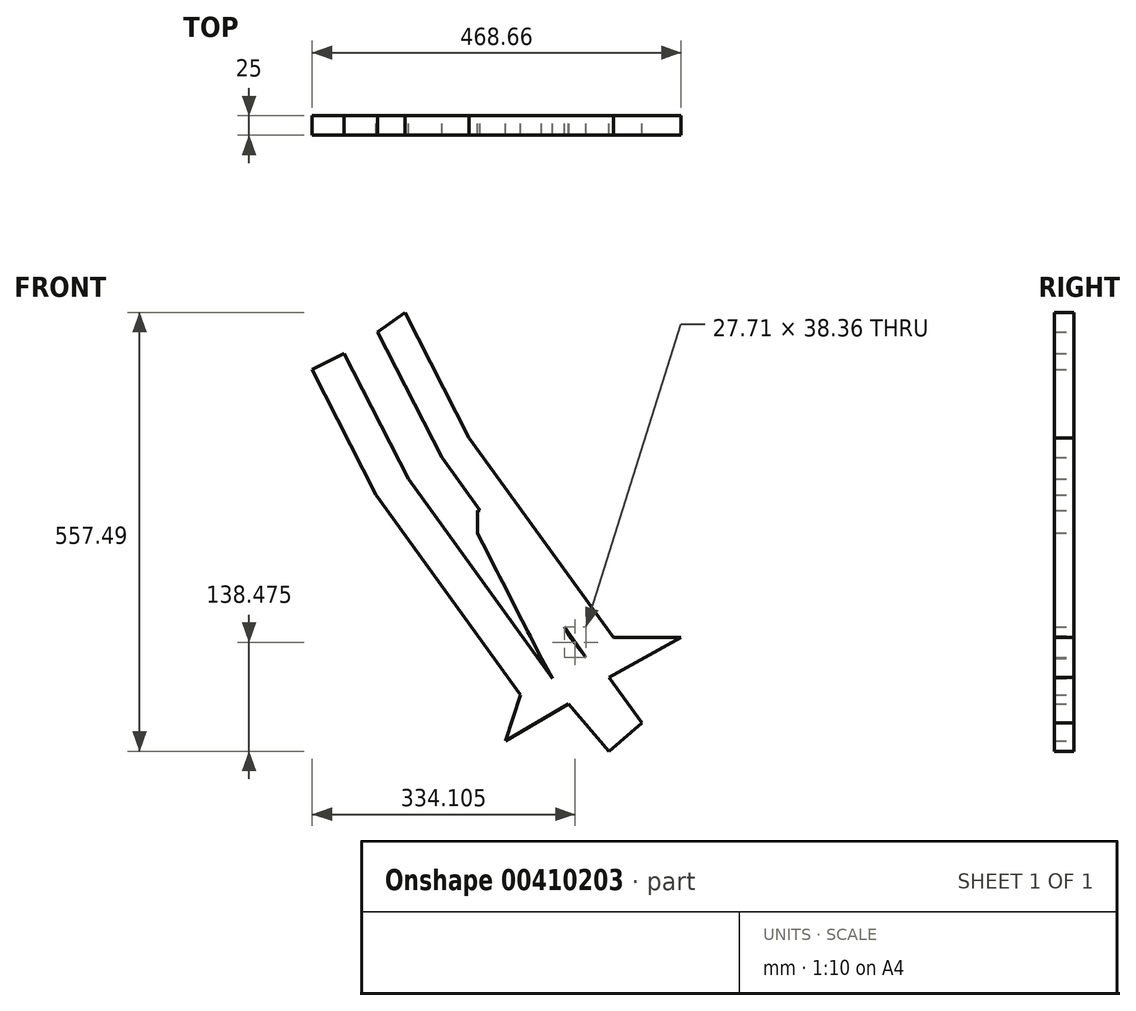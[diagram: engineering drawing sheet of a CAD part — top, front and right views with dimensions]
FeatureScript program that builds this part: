
annotation { "Feature Type Name" : "Feature", "Feature Type Description" : "" }
export const myFeature = defineFeature(function(context is Context, id is Id, definition is map)
    precondition{}
    {
        {
            var Q0;
            Q0=qCreatedBy(makeId("Front.planeOp"),FACE);
            var sketch = newSketch(context, id + "F0", { "sketchPlane" : qUnion([Q0])});
            skLineSegment(sketch, "E0", {"start": v(-19.96, 16.8) * mm, "end": v(14.76, 16.8) * mm});
            skLineSegment(sketch, "E1", {"start": v(14.76, 16.8) * mm, "end": v(-19.96, -11.65) * mm});
            skLineSegment(sketch, "E2", {"start": v(-19.96, -11.65) * mm, "end": v(-19.96, 16.8) * mm});
            skSolve(sketch);
        }
        {
            var Q0;
            Q0=makeQuery(id+"F0.imprint","IMPRINT",FACE,{"disambiguationData":[TD([[makeQuery(id+"F0.imprint","IMPRINT",EDGE,{"derivedFrom":sQuery(id+"F0.wireOp",EDGE,"E0")}),-1.0]])]});
            var sketch = newSketch(context, id + "F1", { "sketchPlane" : qUnion([Q0])});
            skLineSegment(sketch, "E3", {"start": v(14.55, 17.3) * mm, "end": v(36.66, -10.2) * mm});
            skLineSegment(sketch, "E4", {"start": v(36.66, -10.2) * mm, "end": v(71.37, 14.86) * mm});
            skLineSegment(sketch, "E5", {"start": v(71.37, 14.86) * mm, "end": v(157.36, 14.86) * mm});
            skLineSegment(sketch, "E6", {"start": v(157.36, 14.86) * mm, "end": v(65.78, -35.68) * mm});
            skLineSegment(sketch, "E7", {"start": v(65.78, -35.68) * mm, "end": v(107.53, -93.46) * mm});
            skLineSegment(sketch, "E8", {"start": v(107.53, -93.46) * mm, "end": v(65.75, -129.5) * mm});
            skLineSegment(sketch, "E9", {"start": v(65.75, -129.5) * mm, "end": v(14.08, -69.6) * mm});
            skLineSegment(sketch, "E10", {"start": v(14.08, -69.6) * mm, "end": v(-65.47, -116.32) * mm});
            skLineSegment(sketch, "E11", {"start": v(-65.47, -116.32) * mm, "end": v(-46.58, -57.93) * mm});
            skLineSegment(sketch, "E12", {"start": v(-46.58, -57.93) * mm, "end": v(-5.79, -37.1) * mm});
            skLineSegment(sketch, "E13", {"start": v(-5.79, -37.1) * mm, "end": v(-19.96, -11.65) * mm});
            skLineSegment(sketch, "E14", {"start": v(-19.96, -11.65) * mm, "end": v(14.87, 16.9) * mm});
            skSolve(sketch);
        }
        {
            var Q0;
            Q0 = qSketchRegion(id + "F1", true);
            extrude(context, id + "F2", {"entities" : qUnion([Q0]), "depth" : 25 * mm});
        }
        {
            var Q0;
            Q0 = qSketchRegion(id + "F0", true);
            extrude(context, id + "F3", {"entities" : qUnion([Q0]), "operationType" : NewBodyOperationType.ADD, "depth" : 25 * mm});
        }
        {
            var Q0;
            Q0=makeQuery(id+"F2.opExtrude","SWEPT_FACE",FACE,{"disambiguationData":[OSD([sQuery(id+"F1.wireOp",EDGE,"E4")])]});
            var Q1;
            Q1=makeQuery(id+"F2.opExtrude","SWEPT_FACE",FACE,{"disambiguationData":[OSD([sQuery(id+"F1.wireOp",EDGE,"E12")])]});
            extrude(context, id + "F4", {"entities" : qUnion([Q0, Q1]), "operationType" : NewBodyOperationType.ADD, "depth" : 313 * mm});
        }
        {
            var Q0;
            Q0=makeQuery(id+"F4.opExtrude","CAP_FACE",FACE,{"disambiguationData":[OSD([sQuery(id+"F1.wireOp",EDGE,"E4")])],"isStart":false});
            var sketch = newSketch(context, id + "F5", { "sketchPlane" : qUnion([Q0])});
            skLineSegment(sketch, "E15", {"start": v(23.74, 0) * mm, "end": v(10.04, -101.26) * mm});
            skLineSegment(sketch, "E16", {"start": v(10.04, -101.26) * mm, "end": v(-24.91, -10.03) * mm});
            skSolve(sketch);
        }
        {
            var Q0;
            Q0=makeQuery(id+"F4.opExtrude","CAP_FACE",FACE,{"disambiguationData":[OSD([sQuery(id+"F1.wireOp",EDGE,"E12")]),OD(0.0)],"isStart":false});
            var Q1;
            {var subQ0=sQuery(id+"F1.wireOp",EDGE,"E4");Q1=makeQuery(id+"F5.imprint","IMPRINT",FACE,{"disambiguationData":[TD([[makeQuery(id+"F5.imprint","IMPRINT",EDGE,{"derivedFrom":makeQuery(id+"F4.opExtrude","CAP_EDGE",EDGE,{"disambiguationData":[OSD([subQ0]),TDD([makeQuery(id+"F2.opExtrude","CAP_EDGE",EDGE,{"disambiguationData":[OSD([subQ0])],"isStart":true})])],"isStart":false})}),-1.0]])]});}
            var Q2;
            Q2=makeQuery(id+"F3.opExtrude","SWEPT_FACE",FACE,{"disambiguationData":[OSD([sQuery(id+"F0.wireOp",EDGE,"E0")])]});
            var Q3;
            Q3=makeQuery(id+"F3.opExtrude","SWEPT_FACE",FACE,{"disambiguationData":[OSD([sQuery(id+"F0.wireOp",EDGE,"E2")])]});
            extrude(context, id + "F6", {"entities" : qUnion([Q0, Q1, Q2, Q3]), "operationType" : NewBodyOperationType.ADD, "depth" : 179 * mm});
        }
    });
